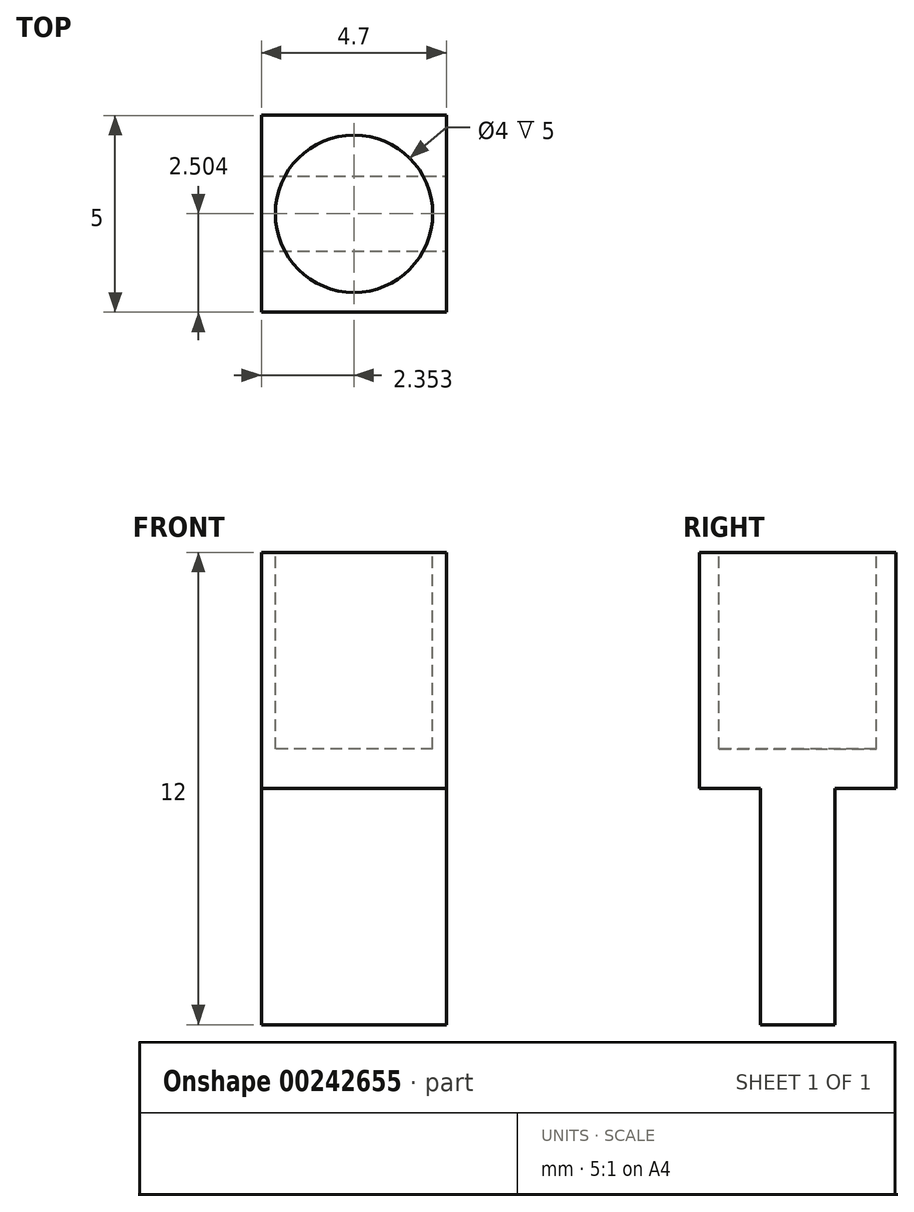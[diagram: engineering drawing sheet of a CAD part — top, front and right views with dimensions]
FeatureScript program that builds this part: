
annotation { "Feature Type Name" : "Feature", "Feature Type Description" : "" }
export const myFeature = defineFeature(function(context is Context, id is Id, definition is map)
    precondition{}
    {
        {
            var Q0;
            Q0=qCreatedBy(makeId("Top.planeOp"),FACE);
            var sketch = newSketch(context, id + "F0", { "sketchPlane" : qUnion([Q0])});
            skLineSegment(sketch, "E0.bottom", {"start": v(-60.74, 39.84) * mm, "end": v(-56.04, 39.84) * mm});
            skLineSegment(sketch, "E0.top", {"start": v(-60.74, 34.84) * mm, "end": v(-56.04, 34.84) * mm});
            skLineSegment(sketch, "E0.left", {"start": v(-60.74, 39.84) * mm, "end": v(-60.74, 34.84) * mm});
            skLineSegment(sketch, "E0.right", {"start": v(-56.04, 39.84) * mm, "end": v(-56.04, 34.84) * mm});
            skSolve(sketch);
        }
        {
            var Q0;
            Q0=makeQuery(id+"F0.imprint","IMPRINT",FACE,{"disambiguationData":[TD([[makeQuery(id+"F0.imprint","IMPRINT",EDGE,{"derivedFrom":sQuery(id+"F0.wireOp",EDGE,"E0.bottom")}),-1.0]])]});
            extrude(context, id + "F1", {"entities" : qUnion([Q0]), "depth" : 6 * mm});
        }
        {
            var Q0;
            Q0=makeQuery(id+"F1.opExtrude","CAP_FACE",FACE,{"disambiguationData":[OSD([sQuery(id+"F0.wireOp",EDGE,"E0.bottom"),sQuery(id+"F0.wireOp",EDGE,"E0.top"),sQuery(id+"F0.wireOp",EDGE,"E0.left"),sQuery(id+"F0.wireOp",EDGE,"E0.right")])],"isStart":false});
            var sketch = newSketch(context, id + "F2", { "sketchPlane" : qUnion([Q0])});
            skCircle(sketch, "E1", {"center": v(-58.39, 37.34) * mm, "radius": 2 * mm});
            skPoint(sketch, "E1.centerSnap0", {"position": v(-56.04, 37.34) * mm});
            skPoint(sketch, "E1.centerSnap1", {"position": v(-58.39, 39.84) * mm});
            skSolve(sketch);
        }
        {
            var Q0;
            Q0=makeQuery(id+"F2.imprint","IMPRINT",FACE,{"disambiguationData":[TD([[makeQuery(id+"F2.imprint","IMPRINT",EDGE,{"derivedFrom":sQuery(id+"F2.wireOp",EDGE,"E1")}),1.0]])]});
            extrude(context, id + "F3", {"entities" : qUnion([Q0]), "operationType" : NewBodyOperationType.REMOVE, "oppositeDirection" : true, "depth" : 5 * mm});
        }
        {
            var Q0;
            Q0=makeQuery(id+"F1.opExtrude","CAP_FACE",FACE,{"disambiguationData":[OSD([sQuery(id+"F0.wireOp",EDGE,"E0.bottom"),sQuery(id+"F0.wireOp",EDGE,"E0.top"),sQuery(id+"F0.wireOp",EDGE,"E0.left"),sQuery(id+"F0.wireOp",EDGE,"E0.right")])],"isStart":true});
            var sketch = newSketch(context, id + "F4", { "sketchPlane" : qUnion([Q0])});
            skLineSegment(sketch, "E2.bottom", {"start": v(-60.74, -38.3) * mm, "end": v(-56.04, -38.3) * mm});
            skLineSegment(sketch, "E2.top", {"start": v(-60.74, -36.4) * mm, "end": v(-56.04, -36.4) * mm});
            skLineSegment(sketch, "E2.left", {"start": v(-60.74, -38.3) * mm, "end": v(-60.74, -36.4) * mm});
            skLineSegment(sketch, "E2.right", {"start": v(-56.04, -38.3) * mm, "end": v(-56.04, -36.4) * mm});
            skPoint(sketch, "E2.middle", {"position": v(-58.39, -37.34) * mm});
            skPoint(sketch, "E2.middle.positionSnap0", {"position": v(-58.39, -34.84) * mm});
            skPoint(sketch, "E2.middle.positionSnap1", {"position": v(-56.04, -37.34) * mm});
            skPoint(sketch, "E2.centerSnap0", {"position": v(-58.39, -34.84) * mm});
            skPoint(sketch, "E2.centerSnap1", {"position": v(-56.04, -37.34) * mm});
            skSolve(sketch);
        }
        {
            var Q0;
            Q0 = qSketchRegion(id + "F4", true);
            extrude(context, id + "F5", {"entities" : qUnion([Q0]), "operationType" : NewBodyOperationType.ADD, "depth" : 6 * mm});
        }
    });
